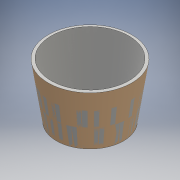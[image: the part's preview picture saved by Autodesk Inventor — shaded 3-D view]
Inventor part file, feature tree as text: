
AUTODESK INVENTOR PART (.ipt)
format: ipt  version: 2016 (Build 200138000, 138)  size: 122,880 bytes
history: native  units: mm
features: sketch x2, plane x1, thicken_offset x1, other x1, loft x1
ambient origin geometry x8: Origin, YZ Plane, XZ Plane, XY Plane, X Axis, Y Axis, Z Axis, Center Point
bodies: Body1 (feature_tree), Body2 (feature_tree)
feature tree (6):
  sketch  "Sketch1"  dims[d0=273.0mm d1=9.52mm]
  plane  "Work Plane1"
  thicken_offset  "Thicken1"
  sketch  "Sketch2"  dims[d2=-178.0mm d3=219.0mm d4=9.52mm d15=0.0mm d16=90.0deg d17=0.0mm d18=90.0deg d19=9.52mm d20=9.52mm]
  other  "Srf1"
  loft  "LoftSrf1"
